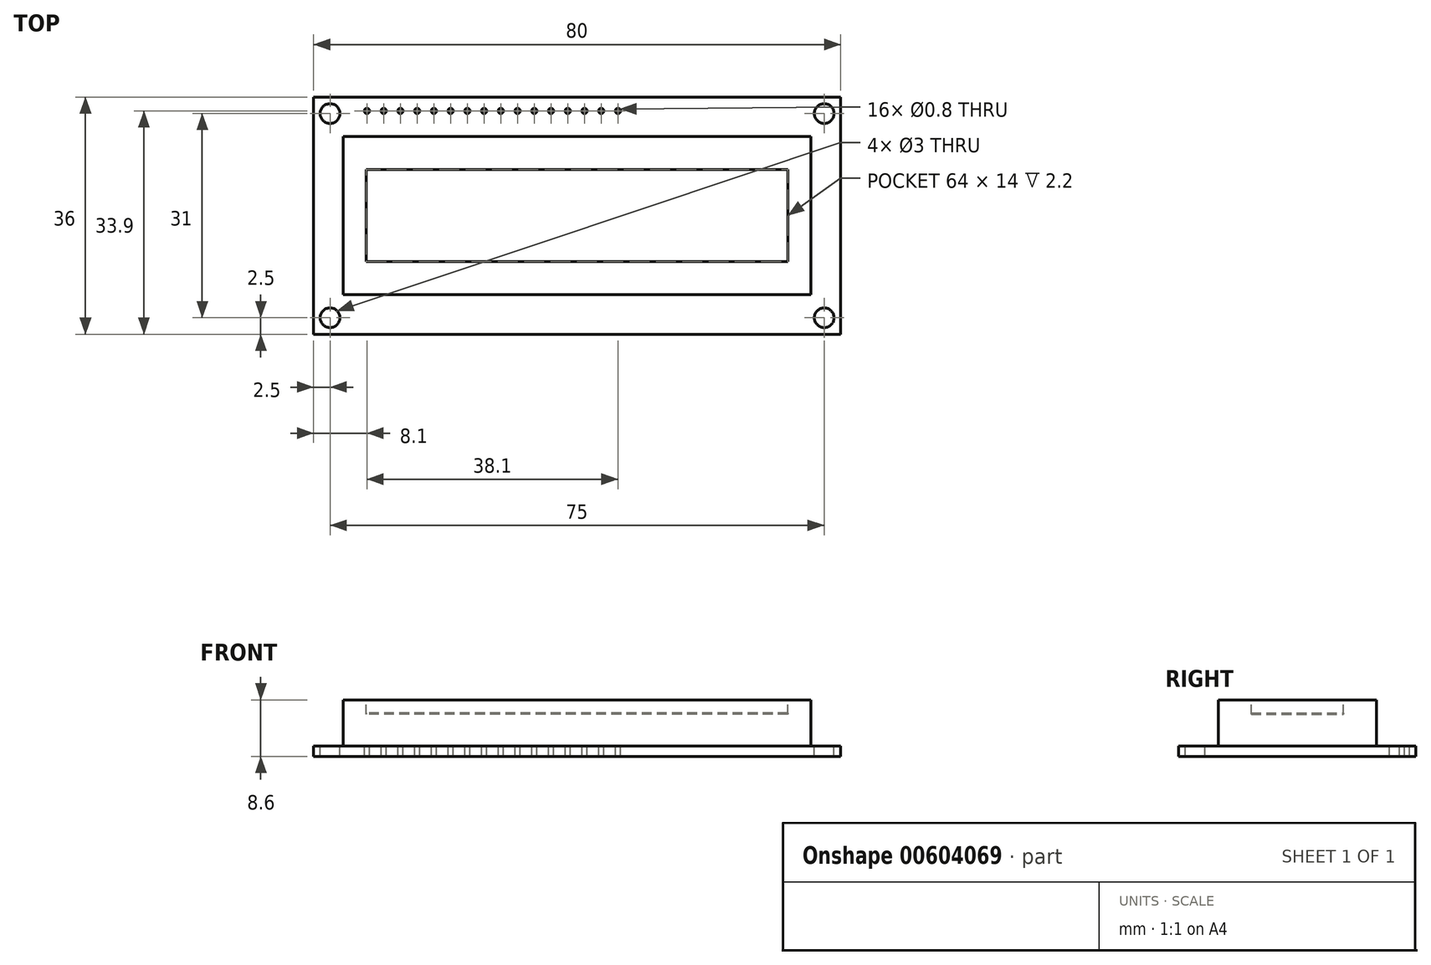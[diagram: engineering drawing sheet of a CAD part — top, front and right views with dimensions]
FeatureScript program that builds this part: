
annotation { "Feature Type Name" : "Feature", "Feature Type Description" : "" }
export const myFeature = defineFeature(function(context is Context, id is Id, definition is map)
    precondition{}
    {
        {
            var Q0;
            Q0=qCreatedBy(makeId("Top.planeOp"),FACE);
            var sketch = newSketch(context, id + "F0", { "sketchPlane" : qUnion([Q0])});
            skLineSegment(sketch, "E0.bottom", {"start": v(40, -18) * mm, "end": v(-40, -18) * mm});
            skLineSegment(sketch, "E0.top", {"start": v(40, 18) * mm, "end": v(-40, 18) * mm});
            skLineSegment(sketch, "E0.left", {"start": v(40, -18) * mm, "end": v(40, 18) * mm});
            skLineSegment(sketch, "E0.right", {"start": v(-40, -18) * mm, "end": v(-40, 18) * mm});
            skPoint(sketch, "E0.middle", {"position": v(0, 0) * mm});
            skCircle(sketch, "E1", {"center": v(-37.5, 15.5) * mm, "radius": 1.5 * mm});
            skCircle(sketch, "E2", {"center": v(-37.5, -15.5) * mm, "radius": 1.5 * mm});
            skCircle(sketch, "E3", {"center": v(37.5, -15.5) * mm, "radius": 1.5 * mm});
            skCircle(sketch, "E4", {"center": v(37.5, 15.5) * mm, "radius": 1.5 * mm});
            skLineSegment(sketch, "E5.bottom", {"start": v(35.5, -12) * mm, "end": v(-35.5, -12) * mm});
            skLineSegment(sketch, "E5.top", {"start": v(35.5, 12) * mm, "end": v(-35.5, 12) * mm});
            skLineSegment(sketch, "E5.left", {"start": v(35.5, -12) * mm, "end": v(35.5, 12) * mm});
            skLineSegment(sketch, "E5.right", {"start": v(-35.5, -12) * mm, "end": v(-35.5, 12) * mm});
            skSolve(sketch);
        }
        {
            var Q0;
            Q0=makeQuery(id+"F0.imprint","IMPRINT",FACE,{"disambiguationData":[TD([[makeQuery(id+"F0.imprint","IMPRINT",EDGE,{"derivedFrom":sQuery(id+"F0.wireOp",EDGE,"E0.bottom")}),-1.0]])]});
            var Q1;
            Q1=makeQuery(id+"F0.imprint","IMPRINT",FACE,{"disambiguationData":[TD([[makeQuery(id+"F0.imprint","IMPRINT",EDGE,{"derivedFrom":sQuery(id+"F0.wireOp",EDGE,"E5.bottom")}),-1.0]])]});
            extrude(context, id + "F1", {"entities" : qUnion([Q0, Q1]), "depth" : -1.6 * mm, "offsetDistance" : 25 * mm});
        }
        {
            var Q0;
            Q0=makeQuery(id+"F0.imprint","IMPRINT",FACE,{"disambiguationData":[TD([[makeQuery(id+"F0.imprint","IMPRINT",EDGE,{"derivedFrom":sQuery(id+"F0.wireOp",EDGE,"E5.bottom")}),-1.0]])]});
            extrude(context, id + "F2", {"entities" : qUnion([Q0]), "depth" : 7 * mm, "offsetDistance" : 25 * mm});
        }
        {
            var Q0;
            Q0=makeQuery(id+"F2.opExtrude","CAP_FACE",FACE,{"disambiguationData":[OSD([sQuery(id+"F0.wireOp",EDGE,"E5.bottom"),sQuery(id+"F0.wireOp",EDGE,"E5.top"),sQuery(id+"F0.wireOp",EDGE,"E5.left"),sQuery(id+"F0.wireOp",EDGE,"E5.right")])],"isStart":false});
            var sketch = newSketch(context, id + "F3", { "sketchPlane" : qUnion([Q0])});
            skLineSegment(sketch, "E6.bottom", {"start": v(32, -7) * mm, "end": v(-32, -7) * mm});
            skLineSegment(sketch, "E6.top", {"start": v(32, 7) * mm, "end": v(-32, 7) * mm});
            skLineSegment(sketch, "E6.left", {"start": v(32, -7) * mm, "end": v(32, 7) * mm});
            skLineSegment(sketch, "E6.right", {"start": v(-32, -7) * mm, "end": v(-32, 7) * mm});
            skPoint(sketch, "E6.middle", {"position": v(0, 0) * mm});
            skSolve(sketch);
        }
        {
            var Q0;
            Q0=makeQuery(id+"F3.imprint","IMPRINT",FACE,{"disambiguationData":[TD([[makeQuery(id+"F3.imprint","IMPRINT",EDGE,{"derivedFrom":sQuery(id+"F3.wireOp",EDGE,"E6.bottom")}),-1.0]])]});
            extrude(context, id + "F4", {"entities" : qUnion([Q0]), "operationType" : NewBodyOperationType.REMOVE, "oppositeDirection" : true, "depth" : 2.2 * mm, "offsetDistance" : 25 * mm});
        }
        {
            var Q0;
            Q0=makeQuery(id+"F4.boolean.opBoolean","COPY",FACE,{"derivedFrom":makeQuery(id+"F4.opExtrude","CAP_FACE",FACE,{"disambiguationData":[OSD([sQuery(id+"F3.wireOp",EDGE,"E6.bottom"),sQuery(id+"F3.wireOp",EDGE,"E6.top"),sQuery(id+"F3.wireOp",EDGE,"E6.left"),sQuery(id+"F3.wireOp",EDGE,"E6.right")])],"isStart":false})});
            extrude(context, id + "F5", {"entities" : qUnion([Q0]), "depth" : .2 * mm, "offsetDistance" : 25 * mm});
        }
        {
            var Q0;
            Q0=makeQuery(id+"F0.imprint","IMPRINT",FACE,{"disambiguationData":[TD([[makeQuery(id+"F0.imprint","IMPRINT",EDGE,{"derivedFrom":sQuery(id+"F0.wireOp",EDGE,"E0.bottom")}),-1.0]])]});
            var sketch = newSketch(context, id + "F6", { "sketchPlane" : qUnion([Q0])});
            skCircle(sketch, "E7", {"center": v(-31.9, 15.9) * mm, "radius": 0.4 * mm});
            skCircle(sketch, "E8", {"center": v(-31.9, 15.9) * mm, "radius": 0.6 * mm});
            skCircle(sketch, "E9.1.0.0", {"center": v(-29.36, 15.9) * mm, "radius": 0.4 * mm});
            skCircle(sketch, "E9.1.0.1", {"center": v(-29.36, 15.9) * mm, "radius": 0.6 * mm});
            skCircle(sketch, "E9.2.0.0", {"center": v(-26.82, 15.9) * mm, "radius": 0.4 * mm});
            skCircle(sketch, "E9.2.0.1", {"center": v(-26.82, 15.9) * mm, "radius": 0.6 * mm});
            skCircle(sketch, "E9.3.0.0", {"center": v(-24.28, 15.9) * mm, "radius": 0.4 * mm});
            skCircle(sketch, "E9.3.0.1", {"center": v(-24.28, 15.9) * mm, "radius": 0.6 * mm});
            skCircle(sketch, "E9.4.0.0", {"center": v(-21.74, 15.9) * mm, "radius": 0.4 * mm});
            skCircle(sketch, "E9.4.0.1", {"center": v(-21.74, 15.9) * mm, "radius": 0.6 * mm});
            skCircle(sketch, "E9.5.0.0", {"center": v(-19.2, 15.9) * mm, "radius": 0.4 * mm});
            skCircle(sketch, "E9.5.0.1", {"center": v(-19.2, 15.9) * mm, "radius": 0.6 * mm});
            skCircle(sketch, "E9.6.0.0", {"center": v(-16.66, 15.9) * mm, "radius": 0.4 * mm});
            skCircle(sketch, "E9.6.0.1", {"center": v(-16.66, 15.9) * mm, "radius": 0.6 * mm});
            skCircle(sketch, "E9.7.0.0", {"center": v(-14.12, 15.9) * mm, "radius": 0.4 * mm});
            skCircle(sketch, "E9.7.0.1", {"center": v(-14.12, 15.9) * mm, "radius": 0.6 * mm});
            skCircle(sketch, "E9.8.0.0", {"center": v(-11.58, 15.9) * mm, "radius": 0.4 * mm});
            skCircle(sketch, "E9.8.0.1", {"center": v(-11.58, 15.9) * mm, "radius": 0.6 * mm});
            skCircle(sketch, "E9.9.0.0", {"center": v(-9.04, 15.9) * mm, "radius": 0.4 * mm});
            skCircle(sketch, "E9.9.0.1", {"center": v(-9.04, 15.9) * mm, "radius": 0.6 * mm});
            skCircle(sketch, "E9.10.0.0", {"center": v(-6.5, 15.9) * mm, "radius": 0.4 * mm});
            skCircle(sketch, "E9.10.0.1", {"center": v(-6.5, 15.9) * mm, "radius": 0.6 * mm});
            skCircle(sketch, "E9.11.0.0", {"center": v(-3.96, 15.9) * mm, "radius": 0.4 * mm});
            skCircle(sketch, "E9.11.0.1", {"center": v(-3.96, 15.9) * mm, "radius": 0.6 * mm});
            skCircle(sketch, "E9.12.0.0", {"center": v(-1.42, 15.9) * mm, "radius": 0.4 * mm});
            skCircle(sketch, "E9.12.0.1", {"center": v(-1.42, 15.9) * mm, "radius": 0.6 * mm});
            skCircle(sketch, "E9.13.0.0", {"center": v(1.12, 15.9) * mm, "radius": 0.4 * mm});
            skCircle(sketch, "E9.13.0.1", {"center": v(1.12, 15.9) * mm, "radius": 0.6 * mm});
            skCircle(sketch, "E9.14.0.0", {"center": v(3.66, 15.9) * mm, "radius": 0.4 * mm});
            skCircle(sketch, "E9.14.0.1", {"center": v(3.66, 15.9) * mm, "radius": 0.6 * mm});
            skCircle(sketch, "E9.15.0.0", {"center": v(6.2, 15.9) * mm, "radius": 0.4 * mm});
            skCircle(sketch, "E9.15.0.1", {"center": v(6.2, 15.9) * mm, "radius": 0.6 * mm});
            skLineSegment(sketch, "E9.direction1", {"start": v(-31.9, 15.9) * mm, "end": v(-29.36, 15.9) * mm, "construction": true});
            skSolve(sketch);
        }
        {
            var Q0;
            Q0=makeQuery(id+"F6.imprint","IMPRINT",FACE,{"disambiguationData":[TD([[makeQuery(id+"F6.imprint","IMPRINT",EDGE,{"derivedFrom":sQuery(id+"F6.wireOp",EDGE,"E7")}),1.0]])]});
            var Q1;
            Q1=makeQuery(id+"F6.imprint","IMPRINT",FACE,{"disambiguationData":[TD([[makeQuery(id+"F6.imprint","IMPRINT",EDGE,{"derivedFrom":sQuery(id+"F6.wireOp",EDGE,"E9.1.0.0")}),1.0]])]});
            var Q2;
            Q2=makeQuery(id+"F6.imprint","IMPRINT",FACE,{"disambiguationData":[TD([[makeQuery(id+"F6.imprint","IMPRINT",EDGE,{"derivedFrom":sQuery(id+"F6.wireOp",EDGE,"E9.2.0.0")}),1.0]])]});
            var Q3;
            Q3=makeQuery(id+"F6.imprint","IMPRINT",FACE,{"disambiguationData":[TD([[makeQuery(id+"F6.imprint","IMPRINT",EDGE,{"derivedFrom":sQuery(id+"F6.wireOp",EDGE,"E9.3.0.0")}),1.0]])]});
            var Q4;
            Q4=makeQuery(id+"F6.imprint","IMPRINT",FACE,{"disambiguationData":[TD([[makeQuery(id+"F6.imprint","IMPRINT",EDGE,{"derivedFrom":sQuery(id+"F6.wireOp",EDGE,"E9.4.0.0")}),1.0]])]});
            var Q5;
            Q5=makeQuery(id+"F6.imprint","IMPRINT",FACE,{"disambiguationData":[TD([[makeQuery(id+"F6.imprint","IMPRINT",EDGE,{"derivedFrom":sQuery(id+"F6.wireOp",EDGE,"E9.5.0.0")}),1.0]])]});
            var Q6;
            Q6=makeQuery(id+"F6.imprint","IMPRINT",FACE,{"disambiguationData":[TD([[makeQuery(id+"F6.imprint","IMPRINT",EDGE,{"derivedFrom":sQuery(id+"F6.wireOp",EDGE,"E9.6.0.0")}),1.0]])]});
            var Q7;
            Q7=makeQuery(id+"F6.imprint","IMPRINT",FACE,{"disambiguationData":[TD([[makeQuery(id+"F6.imprint","IMPRINT",EDGE,{"derivedFrom":sQuery(id+"F6.wireOp",EDGE,"E9.7.0.0")}),1.0]])]});
            var Q8;
            Q8=makeQuery(id+"F6.imprint","IMPRINT",FACE,{"disambiguationData":[TD([[makeQuery(id+"F6.imprint","IMPRINT",EDGE,{"derivedFrom":sQuery(id+"F6.wireOp",EDGE,"E9.8.0.0")}),1.0]])]});
            var Q9;
            Q9=makeQuery(id+"F6.imprint","IMPRINT",FACE,{"disambiguationData":[TD([[makeQuery(id+"F6.imprint","IMPRINT",EDGE,{"derivedFrom":sQuery(id+"F6.wireOp",EDGE,"E9.9.0.0")}),1.0]])]});
            var Q10;
            Q10=makeQuery(id+"F6.imprint","IMPRINT",FACE,{"disambiguationData":[TD([[makeQuery(id+"F6.imprint","IMPRINT",EDGE,{"derivedFrom":sQuery(id+"F6.wireOp",EDGE,"E9.10.0.0")}),1.0]])]});
            var Q11;
            Q11=makeQuery(id+"F6.imprint","IMPRINT",FACE,{"disambiguationData":[TD([[makeQuery(id+"F6.imprint","IMPRINT",EDGE,{"derivedFrom":sQuery(id+"F6.wireOp",EDGE,"E9.11.0.0")}),1.0]])]});
            var Q12;
            Q12=makeQuery(id+"F6.imprint","IMPRINT",FACE,{"disambiguationData":[TD([[makeQuery(id+"F6.imprint","IMPRINT",EDGE,{"derivedFrom":sQuery(id+"F6.wireOp",EDGE,"E9.12.0.0")}),1.0]])]});
            var Q13;
            Q13=makeQuery(id+"F6.imprint","IMPRINT",FACE,{"disambiguationData":[TD([[makeQuery(id+"F6.imprint","IMPRINT",EDGE,{"derivedFrom":sQuery(id+"F6.wireOp",EDGE,"E9.13.0.0")}),1.0]])]});
            var Q14;
            Q14=makeQuery(id+"F6.imprint","IMPRINT",FACE,{"disambiguationData":[TD([[makeQuery(id+"F6.imprint","IMPRINT",EDGE,{"derivedFrom":sQuery(id+"F6.wireOp",EDGE,"E9.14.0.0")}),1.0]])]});
            var Q15;
            Q15=makeQuery(id+"F6.imprint","IMPRINT",FACE,{"disambiguationData":[TD([[makeQuery(id+"F6.imprint","IMPRINT",EDGE,{"derivedFrom":sQuery(id+"F6.wireOp",EDGE,"E9.15.0.0")}),1.0]])]});
            extrude(context, id + "F7", {"entities" : qUnion([Q0, Q1, Q2, Q3, Q4, Q5, Q6, Q7, Q8, Q9, Q10, Q11, Q12, Q13, Q14, Q15]), "operationType" : NewBodyOperationType.REMOVE, "oppositeDirection" : true, "depth" : 25 * mm, "offsetDistance" : 25 * mm});
        }
    });
